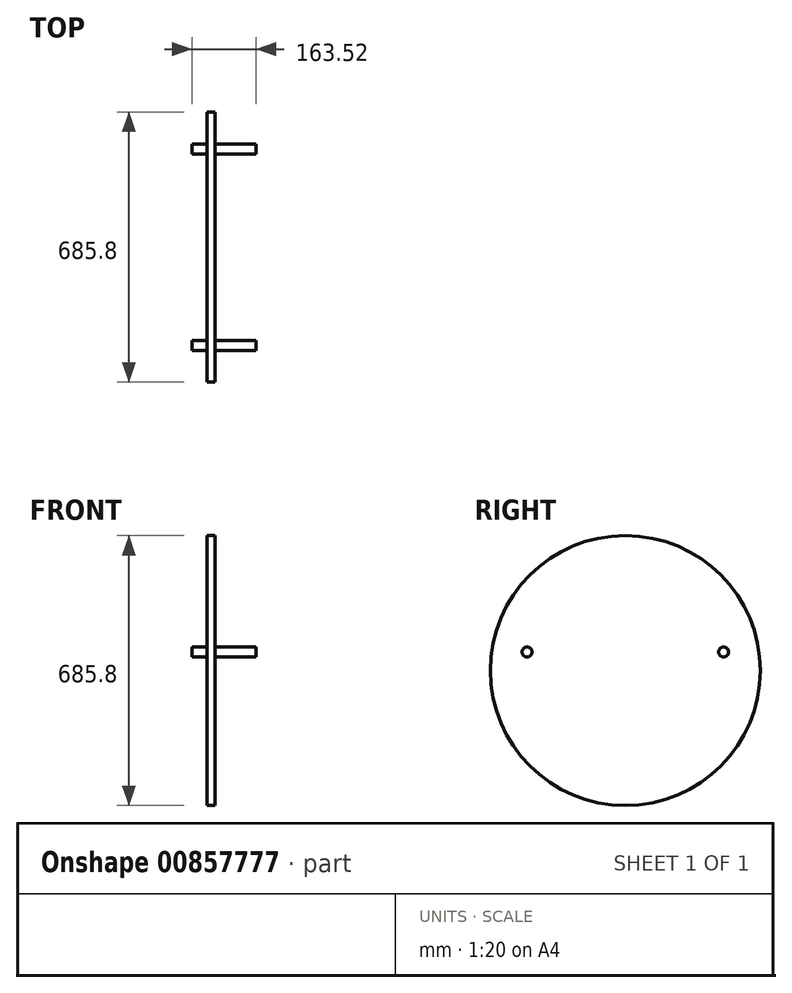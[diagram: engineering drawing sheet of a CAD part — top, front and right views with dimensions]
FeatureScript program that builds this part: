
annotation { "Feature Type Name" : "Feature", "Feature Type Description" : "" }
export const myFeature = defineFeature(function(context is Context, id is Id, definition is map)
    precondition{}
    {
        {
            var Q0;
            Q0=qCreatedBy(makeId("Right.planeOp"),FACE);
            var sketch = newSketch(context, id + "F0", { "sketchPlane" : qUnion([Q0])});
            skCircle(sketch, "E0", {"center": v(0, 0) * mm, "radius": 342.9 * mm});
            skSolve(sketch);
        }
        {
            var Q0;
            Q0=makeQuery(id+"F0.imprint","IMPRINT",FACE,{"disambiguationData":[TD([[makeQuery(id+"F0.imprint","IMPRINT",EDGE,{"derivedFrom":sQuery(id+"F0.wireOp",EDGE,"E0")}),1.0]])]});
            extrude(context, id + "F1", {"entities" : qUnion([Q0]), "oppositeDirection" : true, "depth" : 20.64 * mm});
        }
        {
            var Q0;
            Q0=makeQuery(id+"F1.opExtrude","CAP_FACE",FACE,{"disambiguationData":[OSD([sQuery(id+"F0.wireOp",EDGE,"E0")])],"isStart":false});
            var sketch = newSketch(context, id + "F2", { "sketchPlane" : qUnion([Q0])});
            skCircle(sketch, "E1", {"center": v(249.62, 46.98) * mm, "radius": 12.7 * mm});
            skCircle(sketch, "E2", {"center": v(-249.62, 46.98) * mm, "radius": 12.7 * mm});
            skLineSegment(sketch, "E3", {"start": v(-249.62, 46.98) * mm, "end": v(249.62, 46.98) * mm, "construction": true});
            skLineSegment(sketch, "E4", {"start": v(249.62, 46.98) * mm, "end": v(0, 0) * mm, "construction": true});
            skLineSegment(sketch, "E5", {"start": v(0, 0) * mm, "end": v(-249.62, 46.98) * mm, "construction": true});
            skSolve(sketch);
        }
        {
            var Q0;
            Q0=makeQuery(id+"F2.imprint","IMPRINT",FACE,{"disambiguationData":[TD([[makeQuery(id+"F2.imprint","IMPRINT",EDGE,{"derivedFrom":sQuery(id+"F2.wireOp",EDGE,"E1")}),1.0]])]});
            var Q1;
            Q1=makeQuery(id+"F2.imprint","IMPRINT",FACE,{"disambiguationData":[TD([[makeQuery(id+"F2.imprint","IMPRINT",EDGE,{"derivedFrom":sQuery(id+"F2.wireOp",EDGE,"E2")}),1.0]])]});
            extrude(context, id + "F3", {"entities" : qUnion([Q0, Q1]), "operationType" : NewBodyOperationType.ADD, "oppositeDirection" : true, "depth" : 125.4 * mm});
        }
        {
            var Q0;
            Q0=makeQuery(id+"F2.imprint","IMPRINT",FACE,{"disambiguationData":[TD([[makeQuery(id+"F2.imprint","IMPRINT",EDGE,{"derivedFrom":sQuery(id+"F2.wireOp",EDGE,"E1")}),1.0]])]});
            var Q1;
            Q1=makeQuery(id+"F2.imprint","IMPRINT",FACE,{"disambiguationData":[TD([[makeQuery(id+"F2.imprint","IMPRINT",EDGE,{"derivedFrom":sQuery(id+"F2.wireOp",EDGE,"E2")}),1.0]])]});
            extrude(context, id + "F4", {"entities" : qUnion([Q0, Q1]), "operationType" : NewBodyOperationType.ADD, "depth" : 38.1 * mm});
        }
    });
